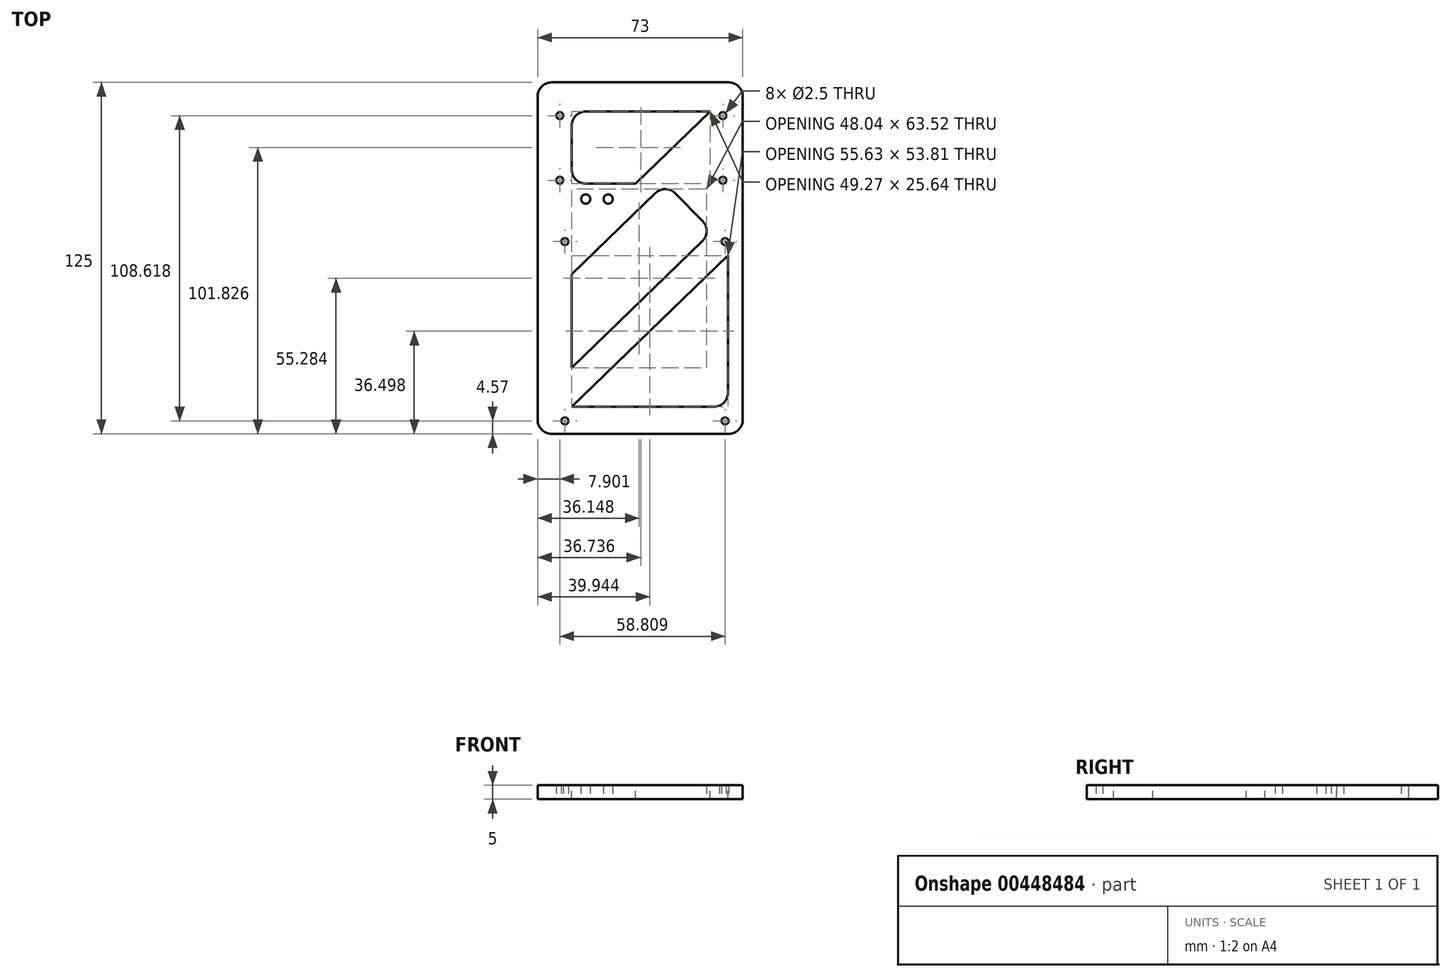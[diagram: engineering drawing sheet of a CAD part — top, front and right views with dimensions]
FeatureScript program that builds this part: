
annotation { "Feature Type Name" : "Feature", "Feature Type Description" : "" }
export const myFeature = defineFeature(function(context is Context, id is Id, definition is map)
    precondition{}
    {
        {
            var Q0;
            Q0=qCreatedBy(makeId("Top.planeOp"),FACE);
            var sketch = newSketch(context, id + "F0", { "sketchPlane" : qUnion([Q0])});
            skLineSegment(sketch, "E0.bottom", {"start": v(28.5, 31.9) * mm, "end": v(-28.5, 31.9) * mm, "construction": true});
            skLineSegment(sketch, "E0.top", {"start": v(28.5, -31.9) * mm, "end": v(-28.5, -31.9) * mm, "construction": true});
            skLineSegment(sketch, "E0.left", {"start": v(28.5, 31.9) * mm, "end": v(28.5, -31.9) * mm, "construction": true});
            skLineSegment(sketch, "E0.right", {"start": v(-28.5, 31.9) * mm, "end": v(-28.5, -31.9) * mm, "construction": true});
            skPoint(sketch, "E0.middle", {"position": v(0, 0) * mm});
            skLineSegment(sketch, "E1.bottom", {"start": v(34.79, -36.47) * mm, "end": v(-38.21, -36.47) * mm});
            skLineSegment(sketch, "E1.top", {"start": v(34.79, 88.53) * mm, "end": v(-38.21, 88.53) * mm});
            skLineSegment(sketch, "E1.left", {"start": v(34.79, -36.47) * mm, "end": v(34.79, 88.53) * mm});
            skLineSegment(sketch, "E1.right", {"start": v(-38.21, -36.47) * mm, "end": v(-38.21, 88.53) * mm});
            skLineSegment(sketch, "E2", {"start": v(-21.09, 47.03) * mm, "end": v(-13.09, 47.03) * mm, "construction": true});
            skLineSegment(sketch, "E3.bottom", {"start": v(-30.3, 76.72) * mm, "end": v(27.7, 76.72) * mm, "construction": true});
            skLineSegment(sketch, "E3.top", {"start": v(-30.3, 53.72) * mm, "end": v(27.7, 53.72) * mm, "construction": true});
            skLineSegment(sketch, "E3.left", {"start": v(-30.3, 76.72) * mm, "end": v(-30.3, 53.72) * mm, "construction": true});
            skLineSegment(sketch, "E3.right", {"start": v(27.7, 76.72) * mm, "end": v(27.7, 53.72) * mm, "construction": true});
            skSolve(sketch);
        }
        {
            var Q0;
            Q0 = qSketchRegion(id + "F0", true);
            extrude(context, id + "F1", {"entities" : qUnion([Q0]), "depth" : 5 * mm, "offsetDistance" : 25 * mm});
        }
        {
            var Q0;
            Q0=sQuery(id+"F0.wireOp",VERTEX,"E3.bottom.start");
            var Q1;
            Q1=sQuery(id+"F0.wireOp",VERTEX,"E3.right.start");
            var Q2;
            Q2=sQuery(id+"F0.wireOp",VERTEX,"E3.right.end");
            var Q3;
            Q3=sQuery(id+"F0.wireOp",VERTEX,"E3.left.end");
            var Q4;
            Q4=makeQuery(id+"F1.opExtrude","SWEPT_BODY",BODY,{"disambiguationData":[OSD([sQuery(id+"F0.wireOp",EDGE,"E1.bottom"),sQuery(id+"F0.wireOp",EDGE,"E1.top"),sQuery(id+"F0.wireOp",EDGE,"E1.left"),sQuery(id+"F0.wireOp",EDGE,"E1.right")])]});
            hole(context, id + "F2", {"style" : HoleStyle.SIMPLE, "endStyle" : HoleEndStyle.THROUGH, "oppositeDirection" : true, "standardTappedOrClearance" : lookupTablePath({ "standard" : "ISO", "engagement" : "75%", "pitch" : "0.5 mm", "size" : "M3", "type" : "Tapped" }), "standardBlindInLast" : lookupTablePath({ "standard" : "ISO", "engagement" : "75%", "pitch" : "0.5 mm", "size" : "M3", "type" : "Tapped" }), "holeDiameter" : 2.5 * mm, "majorDiameter" : 3 * mm, "showTappedDepth" : true, "isTappedThrough" : true, "tappedDepth" : 12 * mm, "tapClearance" : 3, "startFromSketch" : true, "locations" : qUnion([Q0, Q1, Q2, Q3]), "scope" : qUnion([Q4])});
        }
        {
            var Q0;
            Q0=sQuery(id+"F0.wireOp",VERTEX,"E2.start");
            var Q1;
            Q1=sQuery(id+"F0.wireOp",VERTEX,"E2.end");
            var Q2;
            Q2=makeQuery(id+"F1.opExtrude","SWEPT_BODY",BODY,{"disambiguationData":[OSD([sQuery(id+"F0.wireOp",EDGE,"E1.bottom"),sQuery(id+"F0.wireOp",EDGE,"E1.top"),sQuery(id+"F0.wireOp",EDGE,"E1.left"),sQuery(id+"F0.wireOp",EDGE,"E1.right")])]});
            hole(context, id + "F3", {"style" : HoleStyle.SIMPLE, "endStyle" : HoleEndStyle.THROUGH, "oppositeDirection" : true, "standardTappedOrClearance" : lookupTablePath({ "standard" : "ISO", "fit" : "Normal", "size" : "M3", "type" : "Clearance" }), "standardBlindInLast" : lookupTablePath({ "fit" : "Standard", "standard" : "ISO", "size" : "M3", "type" : "Clearance" }), "holeDiameter" : 3.3 * mm, "majorDiameter" : 5 * mm, "isTappedThrough" : true, "tappedDepth" : 12 * mm, "tapClearance" : 3, "startFromSketch" : true, "locations" : qUnion([Q0, Q1]), "scope" : qUnion([Q2])});
        }
        {
            var Q0;
            Q0=sQuery(id+"F0.wireOp",VERTEX,"E0.right.start");
            var Q1;
            Q1=sQuery(id+"F0.wireOp",VERTEX,"E0.bottom.start");
            var Q2;
            Q2=sQuery(id+"F0.wireOp",VERTEX,"E0.left.end");
            var Q3;
            Q3=sQuery(id+"F0.wireOp",VERTEX,"E0.right.end");
            var Q4;
            Q4=makeQuery(id+"F1.opExtrude","SWEPT_BODY",BODY,{"disambiguationData":[OSD([sQuery(id+"F0.wireOp",EDGE,"E1.bottom"),sQuery(id+"F0.wireOp",EDGE,"E1.top"),sQuery(id+"F0.wireOp",EDGE,"E1.left"),sQuery(id+"F0.wireOp",EDGE,"E1.right")])]});
            hole(context, id + "F4", {"style" : HoleStyle.SIMPLE, "endStyle" : HoleEndStyle.THROUGH, "oppositeDirection" : true, "standardTappedOrClearance" : lookupTablePath({ "standard" : "ISO", "engagement" : "75%", "pitch" : "0.5 mm", "size" : "M3", "type" : "Tapped" }), "standardBlindInLast" : lookupTablePath({ "standard" : "ISO", "engagement" : "75%", "pitch" : "0.5 mm", "size" : "M3", "type" : "Tapped" }), "holeDiameter" : 2.5 * mm, "majorDiameter" : 3 * mm, "showTappedDepth" : true, "isTappedThrough" : true, "tappedDepth" : 12 * mm, "tapClearance" : 3, "startFromSketch" : true, "locations" : qUnion([Q0, Q1, Q2, Q3]), "scope" : qUnion([Q4])});
        }
        {
            var Q0;
            Q0=makeQuery(id+"F1.opExtrude","CAP_FACE",FACE,{"disambiguationData":[OSD([sQuery(id+"F0.wireOp",EDGE,"E1.bottom"),sQuery(id+"F0.wireOp",EDGE,"E1.top"),sQuery(id+"F0.wireOp",EDGE,"E1.left"),sQuery(id+"F0.wireOp",EDGE,"E1.right")])],"isStart":false});
            var sketch = newSketch(context, id + "F5", { "sketchPlane" : qUnion([Q0])});
            skLineSegment(sketch, "E4", {"start": v(7.31, 52.62) * mm, "end": v(-26.08, 20.32) * mm});
            skLineSegment(sketch, "E5", {"start": v(-26.08, 20.32) * mm, "end": v(-26.08, -12.95) * mm});
            skLineSegment(sketch, "E6", {"start": v(-26.08, -12.95) * mm, "end": v(24.05, 35.55) * mm});
            skLineSegment(sketch, "E7", {"start": v(24.05, 35.55) * mm, "end": v(7.31, 52.62) * mm});
            skLineSegment(sketch, "E8", {"start": v(-26.08, -26.88) * mm, "end": v(29.55, 26.94) * mm});
            skLineSegment(sketch, "E9", {"start": v(29.55, 26.94) * mm, "end": v(29.55, -26.88) * mm});
            skLineSegment(sketch, "E10", {"start": v(29.55, -26.88) * mm, "end": v(-26.08, -26.88) * mm});
            skLineSegment(sketch, "E11", {"start": v(23.16, 78.17) * mm, "end": v(-3.34, 52.54) * mm});
            skLineSegment(sketch, "E12", {"start": v(-3.34, 52.54) * mm, "end": v(-26.1, 52.54) * mm});
            skPoint(sketch, "E13.end.orphan", {"position": v(-22.38, 78.17) * mm});
            skPoint(sketch, "E14.start.orphan", {"position": v(0.4, 78.17) * mm});
            skLineSegment(sketch, "E15", {"start": v(-26.1, 52.54) * mm, "end": v(-26.1, 78.17) * mm});
            skLineSegment(sketch, "E16", {"start": v(-26.1, 78.17) * mm, "end": v(23.16, 78.17) * mm});
            skSolve(sketch);
        }
        {
            var Q0;
            Q0=makeQuery(id+"F5.imprint","IMPRINT",FACE,{"disambiguationData":[TD([[makeQuery(id+"F5.imprint","IMPRINT",EDGE,{"derivedFrom":sQuery(id+"F5.wireOp",EDGE,"E4")}),1.0]])]});
            var Q1;
            Q1=makeQuery(id+"F5.imprint","IMPRINT",FACE,{"disambiguationData":[TD([[makeQuery(id+"F5.imprint","IMPRINT",EDGE,{"derivedFrom":sQuery(id+"F5.wireOp",EDGE,"E8")}),-1.0]])]});
            var Q2;
            Q2=makeQuery(id+"F5.imprint","IMPRINT",FACE,{"disambiguationData":[TD([[makeQuery(id+"F5.imprint","IMPRINT",EDGE,{"derivedFrom":sQuery(id+"F5.wireOp",EDGE,"E14")}),-1.0]])]});
            var Q3;
            Q3=makeQuery(id+"F5.imprint","IMPRINT",FACE,{"disambiguationData":[TD([[makeQuery(id+"F5.imprint","IMPRINT",EDGE,{"derivedFrom":sQuery(id+"F5.wireOp",EDGE,"E11")}),-1.0]])]});
            extrude(context, id + "F6", {"entities" : qUnion([Q0, Q1, Q2, Q3]), "operationType" : NewBodyOperationType.REMOVE, "oppositeDirection" : true, "depth" : 25 * mm, "offsetDistance" : 25 * mm});
        }
        {
            var Q0;
            Q0=makeQuery(id+"F1.opExtrude","SWEPT_EDGE",EDGE,{"disambiguationData":[OSD([sQuery(id+"F0.wireOp",EDGE,"E1.top"),sQuery(id+"F0.wireOp",EDGE,"E1.right")])]});
            var Q1;
            Q1=makeQuery(id+"F1.opExtrude","SWEPT_EDGE",EDGE,{"disambiguationData":[OSD([sQuery(id+"F0.wireOp",EDGE,"E1.top"),sQuery(id+"F0.wireOp",EDGE,"E1.left")])]});
            var Q2;
            Q2=makeQuery(id+"F1.opExtrude","SWEPT_EDGE",EDGE,{"disambiguationData":[OSD([sQuery(id+"F0.wireOp",EDGE,"E1.bottom"),sQuery(id+"F0.wireOp",EDGE,"E1.left")])]});
            var Q3;
            Q3=makeQuery(id+"F1.opExtrude","SWEPT_EDGE",EDGE,{"disambiguationData":[OSD([sQuery(id+"F0.wireOp",EDGE,"E1.bottom"),sQuery(id+"F0.wireOp",EDGE,"E1.right")])]});
            var Q4;
            Q4=makeQuery(id+"F6.boolean.opBoolean","COPY",EDGE,{"derivedFrom":makeQuery(id+"F6.opExtrude","SWEPT_EDGE",EDGE,{"disambiguationData":[OSD([sQuery(id+"F5.wireOp",EDGE,"E12"),sQuery(id+"F5.wireOp",EDGE,"E15")])]})});
            var Q5;
            Q5=makeQuery(id+"F6.boolean.opBoolean","COPY",EDGE,{"derivedFrom":makeQuery(id+"F6.opExtrude","SWEPT_EDGE",EDGE,{"disambiguationData":[OSD([sQuery(id+"F5.wireOp",EDGE,"E15"),sQuery(id+"F5.wireOp",EDGE,"E16")])]})});
            var Q6;
            Q6=makeQuery(id+"F6.boolean.opBoolean","COPY",EDGE,{"derivedFrom":makeQuery(id+"F6.opExtrude","SWEPT_EDGE",EDGE,{"disambiguationData":[OSD([sQuery(id+"F5.wireOp",EDGE,"E6"),sQuery(id+"F5.wireOp",EDGE,"E7")])]})});
            var Q7;
            Q7=makeQuery(id+"F6.boolean.opBoolean","COPY",EDGE,{"derivedFrom":makeQuery(id+"F6.opExtrude","SWEPT_EDGE",EDGE,{"disambiguationData":[OSD([sQuery(id+"F5.wireOp",EDGE,"E4"),sQuery(id+"F5.wireOp",EDGE,"E7")])]})});
            var Q8;
            Q8=makeQuery(id+"F6.boolean.opBoolean","COPY",EDGE,{"derivedFrom":makeQuery(id+"F6.opExtrude","SWEPT_EDGE",EDGE,{"disambiguationData":[OSD([sQuery(id+"F5.wireOp",EDGE,"E9"),sQuery(id+"F5.wireOp",EDGE,"E10")])]})});
            fillet(context, id + "F7", {"entities" : qUnion([Q0, Q1, Q2, Q3, Q4, Q5, Q6, Q7, Q8]), "radius" : 5 * mm, "tangentPropagation" : true, "allowEdgeOverflow" : false});
        }
    });
